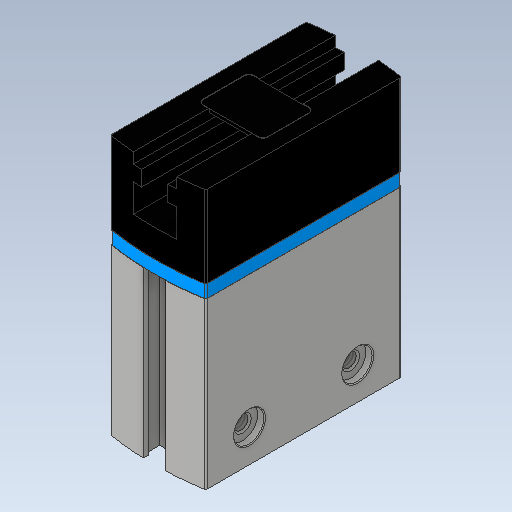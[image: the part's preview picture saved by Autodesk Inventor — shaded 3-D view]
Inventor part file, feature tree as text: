
AUTODESK INVENTOR PART (.ipt)
format: ipt  version: 2020 (Build 240168000, 168)  size: 344,576 bytes
history: native  units: mm
features: other x35, sketch x15, extrude x9, revolve x4, thread x4, hole x2
ambient origin geometry x8: Origin, YZ Plane, XZ Plane, XY Plane, X Axis, Y Axis, Z Axis, Center Point
bodies: Solid1 (feature_tree)
feature tree (69):
  extrude  "Extrusion1"  Depth=3.0mm TaperAngle=0.0deg
  extrude  "Extrusion2"  Depth=66.0mm TaperAngle=0.0deg
  extrude  "Extrusion3"  Depth=0.1mm TaperAngle=0.0deg
  extrude  "Extrusion4"  Depth=18.042mm TaperAngle=0.0deg
  extrude  "Extrusion5"  Depth=18.042mm TaperAngle=0.0deg
  extrude  "Extrusion6"  TaperAngle=360.0deg  [1 undecoded]
  revolve  "Revolution1"  Angle=360.0deg
  thread  "Thread1"  [1 undecoded]
  revolve  "Revolution2"  [1 undecoded]
  thread  "Thread2"  [1 undecoded]
  extrude  "Extrusion7"  TaperAngle=0.0deg  [1 undecoded]
  hole  "Hole1"  [1 undecoded]
  hole  "Hole2"  [1 undecoded]
  revolve  "Revolution3"  [1 undecoded]
  thread  "Thread3"  [1 undecoded]
  revolve  "Revolution4"  [1 undecoded]
  thread  "Thread4"  [1 undecoded]
  extrude  "Extrusion8"  [1 undecoded]
  extrude  "Extrusion9"  [1 undecoded]
  other  "GEHAEUSE_XY"
  other  "GEHAEUSE_YZ"
  other  "GEHAEUSE_ZX"
  other  "GEHAEUSE_X"
  other  "GEHAEUSE_Y"
  other  "GEHAEUSE_Z"
  other  "GEHAEUSE_Center"
  other  "TO_GREIF_XY"
  other  "TO_GREIF_YZ"
  other  "TO_GREIF_ZX"
  other  "TO_GREIF_X"
  other  "TO_GREIF_Y"
  other  "TO_GREIF_Z"
  other  "TO_GREIF_Center"
  other  "TO_GREIF_R_XY"
  other  "TO_GREIF_R_YZ"
  other  "TO_GREIF_R_ZX"
  other  "TO_GREIF_R_X"
  other  "TO_GREIF_R_Y"
  other  "TO_GREIF_R_Z"
  other  "TO_GREIF_R_Center"
  other  "TO_ZBH_1_XY"
  other  "TO_ZBH_1_YZ"
  other  "TO_ZBH_1_ZX"
  other  "TO_ZBH_1_X"
  other  "TO_ZBH_1_Y"
  other  "TO_ZBH_1_Z"
  other  "TO_ZBH_1_Center"
  other  "TO_ZBH_2_XY"
  other  "TO_ZBH_2_YZ"
  other  "TO_ZBH_2_ZX"
  other  "TO_ZBH_2_X"
  other  "TO_ZBH_2_Y"
  other  "TO_ZBH_2_Z"
  other  "TO_ZBH_2_Center"
  sketch  "Sketch_1"  dims[d0=38.1mm d1=0.0mm d2=3.0mm d3=0.0mm]
  sketch  "Sketch_2"  dims[d4=18.9mm d5=0.0mm d6=66.0mm d7=0.0mm]
  sketch  "Sketch_3"  dims[d8=0.8mm d9=0.0mm d10=0.1mm d11=0.0mm]
  sketch  "Sketch_4"  dims[d12=360.0deg d13=18.042mm d14=0.0mm]
  sketch  "Sketch_5"  dims[d15=360.0deg d16=18.042mm d17=0.0mm]
  sketch  "Sketch_15"
  sketch  "Sketch_6"  dims[d18=3.0mm d19=0.0mm]
  sketch  "Sketch_7"  dims[d20=2.459mm d21=6.0mm d22=3.0mm d23=2.0mm d24=90.0deg d25=7.0mm d26=0.0mm]
  sketch  "Sketch_8"  dims[d27=2.459mm d28=6.0mm d29=3.0mm d30=2.0mm d31=90.0deg d32=7.0mm d33=0.0mm d34=360.0deg]
  sketch  "Sketch10"  dims[d35=5.521mm d36=0.0mm d37=360.0deg d38=5.521mm d39=0.0mm]
  sketch  "Sketch11"  dims[d40=1.5mm d41=0.0mm d42=1.5mm d43=0.0mm d44=0.0mm]
  sketch  "Sketch_11"  dims[d45=0.0mm d46=0.0mm]
  sketch  "Sketch_12"
  sketch  "Sketch_17"
  sketch  "Sketch_18"
note: 13 required parameter values undecoded (feature->parameter linkage not recoverable at this tier; creation-order binding heuristic only, values carry confidence <= 0.55)